# Revit family: Sanitary_Installation-Systems_AXOR_01005XXX-AXOR-iBox-universal-Base-set-fo_NEWwww
name_source: partatom
category: Plumbing Fixtures
revit_build: Autodesk Revit 2018 (Build: 20170223_1515(x64)
units: mm (PartAtom-declared; Revit-internal decimal feet)

## family parameters
Cut with Voids When Loaded = Yes
Host = Face
OmniClass Number = 23.31.17.29
OmniClass Title = Shower Drains
Part Type = Normal
Room Calculation Point = No
Round Connector Dimension = Use Diameter
Shared = No

## types (1)
- 01005XXX AXOR iBox universal Base set for finish sets for flat installation
    BIMobject category = Installation Systems
    Connector Description = Water Outlet 50 mm
    Default Elevation = 1219 mm
    Description = AXOR iBox universal Base set for finish sets for flat installation
    Design country = Germany
    Diameter = 50  [stored 0.164042 ft]
    Edition number = 1
    IFC Classification = Sanitary Terminal
    Manufacturer = AXOR
    Manufacturer country = Germany
    Manufacturer name = AXOR
    Material 1 = AXOR - Plastic - Dark Grey
    Material 2 = AXOR - Plastic - Black
    Material 3 = AXOR - Plastic - Grey
    Model = 01005XXX
    OmniClass Code = 23-31 17 29
    OmniClass Description = Shower Drains
    Product Guid = e966ffb3-a6ed-450f-a1f2-3482397a930b
    Product SKU = 01005XXX
    Product data url = https://bimobject.com
    Product name = 01005XXX AXOR iBox universal Base set for finish sets for flat installation
    Product url = https://www.axor-design.com
    QR code = https://bimobject.com
    URL = https://www.axor-design.com

note: [stored X ft] marks values corroborated as IEEE doubles in the binary element streams (Revit-internal decimal feet)

## geometry (parser evidence)
native form markers: Sweep x4
no freeform markers — native parametric forms only
